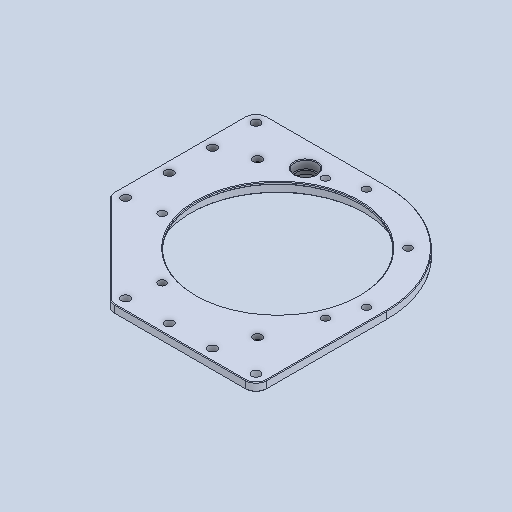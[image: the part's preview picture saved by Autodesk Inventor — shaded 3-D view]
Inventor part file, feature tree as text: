
AUTODESK INVENTOR PART (.ipt)
format: ipt  version: 2023.2 (Build 272271000, 271)  size: 248,320 bytes
history: native  units: in
note: dims shown in document units (in); Inventor stores cm internally (conversion verified against a paired STEP export)
features: chamfer x1
ambient origin geometry x8: Origin, YZ Plane, XZ Plane, XY Plane, X Axis, Y Axis, Z Axis, Center Point
bodies: Solid1 (feature_tree)
feature tree (1):
  chamfer  "Chamfer3"  [1 undecoded]
note: 1 required parameter value undecoded (feature->parameter linkage not recoverable at this tier; creation-order binding heuristic only, values carry confidence <= 0.55)
